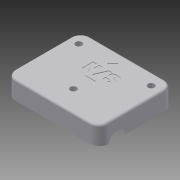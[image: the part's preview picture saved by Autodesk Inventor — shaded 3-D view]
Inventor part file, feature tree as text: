
AUTODESK INVENTOR PART (.ipt)
format: ipt  version: 2014 (Build 180170000, 170)  size: 333,312 bytes
history: native  units: in
note: dims shown in document units (in); Inventor stores cm internally (conversion verified against a paired STEP export)
features: sketch x9, extrude x5, mirror x3, plane x2, other x2, revolve x2, fillet x2, hole x1, emboss x1
ambient origin geometry x8: Origin, YZ Plane, XZ Plane, XY Plane, X Axis, Y Axis, Z Axis, Center Point
bodies: Solid1 (feature_tree)
feature tree (27):
  sketch  "Sketch1"  dims[d0=2.5in d1=2.0in]
  extrude  "Extrusion1"  Depth=2.0in
  plane  "Work Plane1"
  plane  "Work Plane2"
  extrude  "Extrusion2"  TaperAngle=120.0deg  [1 undecoded]
  mirror  "Mirror2"
  extrude  "Extrusion4"  TaperAngle=120.0deg  [1 undecoded]
  sketch  "Sketch6"  dims[d6=0.5in d7=0.0in d9=-0.2061in]
  other  "Work Axis1"
  revolve  "Revolution1"  [1 undecoded]
  mirror  "Mirror3"
  sketch  "Sketch11"  dims[d10=0.38in d11=0.5in d12=0.0in]
  other  "Work Axis2"
  revolve  "Revolution4"  [1 undecoded]
  extrude  "Extrusion5"  Depth=0.28in
  extrude  "Extrusion6"  Depth=0.105in
  mirror  "Mirror4"
  hole  "Hole1"  [1 undecoded]
  fillet  "Fillet1"  Radius=0.08in
  emboss  "Emboss1"
  fillet  "Fillet2"  [1 undecoded]
  sketch  "Sketch2"  dims[d2=0.8in d3=120.0deg]
  sketch  "Sketch5"  dims[d4=150.0deg d5=120.0deg]
  sketch  "Sketch12"  dims[d13=90.0deg d18=0.28in]
  sketch  "Sketch13"  dims[d19=0.8in d20=0.0in d21=0.105in]
  sketch  "Sketch14"  dims[d22=90.0deg d23=0.075in d33=0.08in d34=180.0deg]
  sketch  "Sketch15"  dims[d35=2.0in d36=0.025in d37=0.025in d38=0.05in d39=0.0in d40=1.25in d41=0.025in d42=0.025in d43=0.05in d44=0.0in d45=0.425in d46=0.83in d47=0.173in d48=0.75in d49=0.405in d50=0.25in d51=0.5635in d52=1.0in d53=0.8108in d54=0.25in d55=0.0156in d56=0.0in d57=0.0625in]
note: 6 required parameter values undecoded (feature->parameter linkage not recoverable at this tier; creation-order binding heuristic only, values carry confidence <= 0.55)